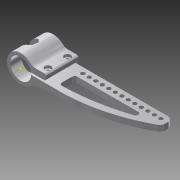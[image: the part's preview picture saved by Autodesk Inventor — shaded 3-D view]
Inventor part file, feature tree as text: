
AUTODESK INVENTOR PART (.ipt)
format: ipt  version: 2015 (Build 190159000, 159)  size: 229,376 bytes
history: native  units: mm
features: sketch x5, fillet x4, extrude x3, hole x2
ambient origin geometry x8: Origin, YZ Plane, XZ Plane, XY Plane, X Axis, Y Axis, Z Axis, Center Point
bodies: Solid1 (feature_tree)
feature tree (14):
  extrude  "Extrusion1"  Depth=42.0mm
  hole  "Hole1"  [1 undecoded]
  hole  "Hole2"  [1 undecoded]
  sketch  "Sketch3"  dims[d2=168.0mm d3=9.0mm]
  fillet  "Fillet1"  Radius=39.0mm
  sketch  "Sketch4"  dims[d4=50.0mm d7=3.0mm d8=39.0mm]
  extrude  "Extrusion3"  Depth=3.0mm
  extrude  "Extrusion4"  Depth=10.0mm
  fillet  "Fillet2"  Radius=50.0mm
  fillet  "Fillet3"  Radius=2.5mm
  fillet  "Fillet4"  Radius=17.0mm
  sketch  "Sketch1"  dims[d0=32.0mm d1=42.0mm]
  sketch  "Sketch5"  dims[d9=9.0mm d10=3.0mm]
  sketch  "Sketch8"  dims[d11=39.0mm d12=10.0mm d13=50.0mm d14=0.0mm d15=10.0mm d16=7.0mm d17=5.5mm d18=6.0mm d19=10.0mm d20=4.0mm d21=90.0deg d22=8.0mm d23=20.594885mm d24=10.0mm d25=7.0mm d26=5.5mm d27=6.0mm d28=10.0mm d29=4.0mm d30=90.0deg d31=8.0mm d32=20.594885mm d40=2.5mm d41=17.0mm d42=40.0mm d43=16.0mm d44=40.0mm d45=8.0mm d46=10.0mm d47=0.0mm d49=50.0mm d50=17.0mm d54=4.0mm d55=8.5mm d56=6.2mm d57=130.0mm d59=10.0mm d60=10.0mm d62=10.0mm d66=130.0mm d68=10.0mm d69=10.0mm d70=0.0mm d71=4.0mm d72=4.0mm d73=120.0mm d74=23.975256mm d75=8.0mm]
note: 2 required parameter values undecoded (feature->parameter linkage not recoverable at this tier; creation-order binding heuristic only, values carry confidence <= 0.55)
